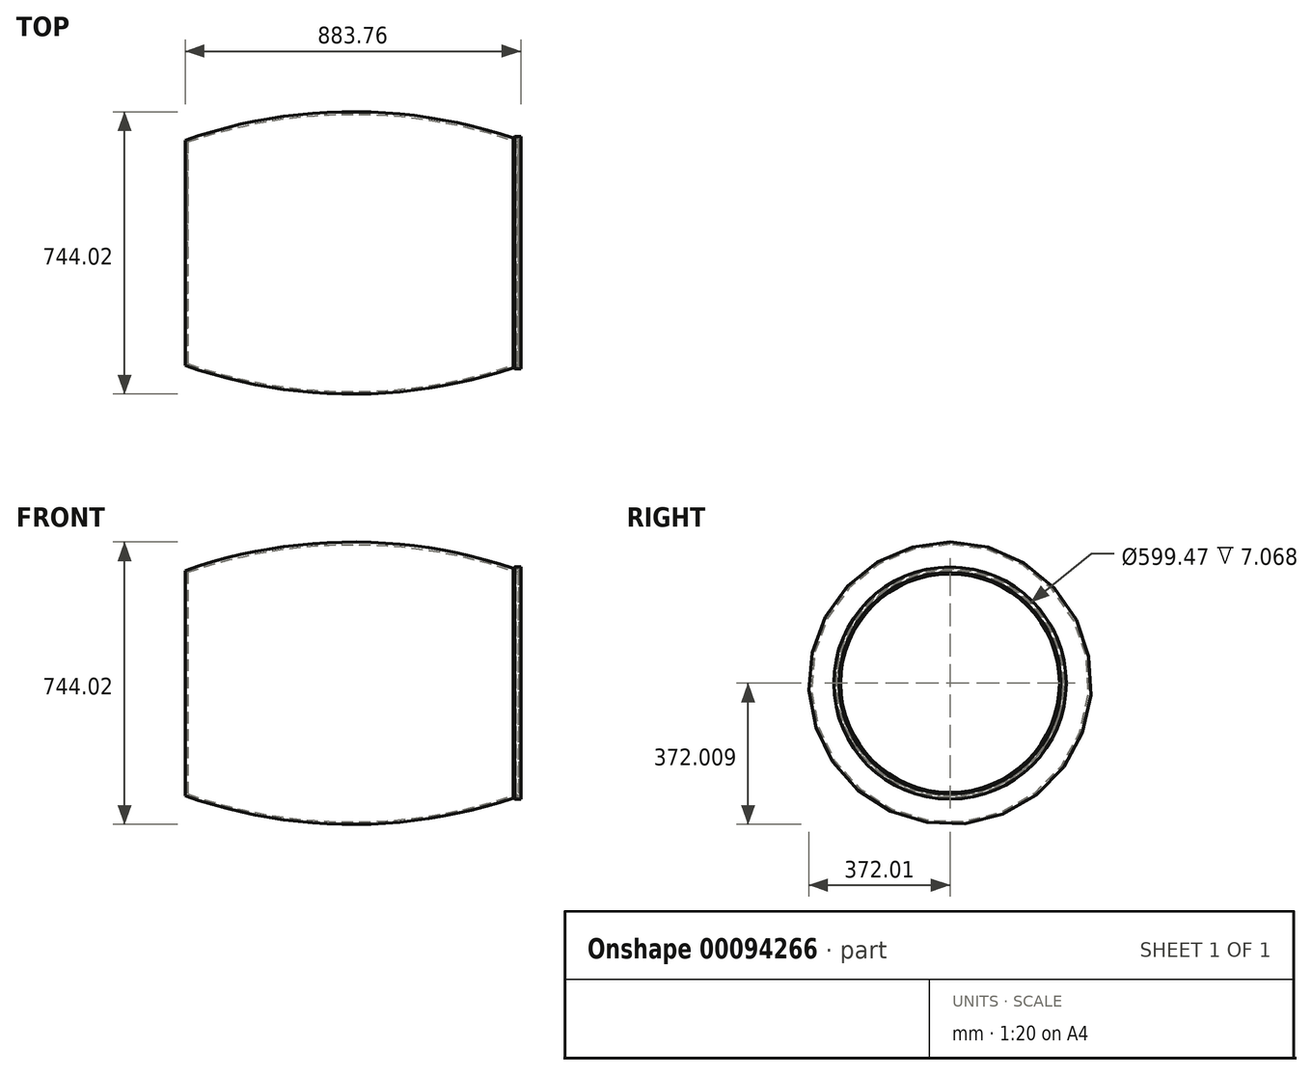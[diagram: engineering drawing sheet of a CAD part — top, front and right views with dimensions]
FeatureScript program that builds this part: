
annotation { "Feature Type Name" : "Feature", "Feature Type Description" : "" }
export const myFeature = defineFeature(function(context is Context, id is Id, definition is map)
    precondition{}
    {
        {
            var Q0;
            Q0=qCreatedBy(makeId("Front.planeOp"),FACE);
            var sketch = newSketch(context, id + "F0", { "sketchPlane" : qUnion([Q0])});
            skLineSegment(sketch, "E0", {"start": v(-396.66, -91.94) * mm, "end": v(466.94, -91.94) * mm});
            skLineSegment(sketch, "E1", {"start": v(466.94, -91.94) * mm, "end": v(466.94, 200.16) * mm});
            skLineSegment(sketch, "E2", {"start": v(-396.66, -91.94) * mm, "end": v(-396.66, 200.16) * mm});
            skLineSegment(sketch, "E3", {"start": v(466.94, 200.16) * mm, "end": v(474.4, 203.75) * mm});
            skLineSegment(sketch, "E4", {"start": v(474.4, 203.75) * mm, "end": v(474.4, 207.8) * mm});
            skLineSegment(sketch, "E5", {"start": v(474.4, 207.8) * mm, "end": v(467.33, 207.8) * mm});
            skLineSegment(sketch, "E6", {"start": v(467.33, 207.8) * mm, "end": v(463.3, 203.17) * mm});
            skArc(sketch, "E7", {"start": v(463.3, 203.17) * mm, "mid": v(33.07, 273.7) * mm, "end": v(-396.66, 200.16) * mm});
            skLineSegment(sketch, "E8.0", {"start": v(-403, -91.94) * mm, "end": v(-403, 204.66) * mm});
            skArc(sketch, "E8.1", {"start": v(461.31, 210.55) * mm, "mid": v(28.66, 280.04) * mm, "end": v(-403, 204.66) * mm});
            skLineSegment(sketch, "E8.2", {"start": v(464.44, 214.14) * mm, "end": v(461.31, 210.55) * mm});
            skLineSegment(sketch, "E8.3", {"start": v(473.3, -91.94) * mm, "end": v(473.3, 196.17) * mm});
            skLineSegment(sketch, "E8.4", {"start": v(473.3, 196.17) * mm, "end": v(480.75, 199.76) * mm});
            skLineSegment(sketch, "E8.5", {"start": v(480.75, 199.76) * mm, "end": v(480.75, 214.14) * mm});
            skLineSegment(sketch, "E8.6", {"start": v(480.75, 214.14) * mm, "end": v(464.44, 214.14) * mm});
            skLineSegment(sketch, "E9", {"start": v(466.94, -91.94) * mm, "end": v(473.3, -91.94) * mm});
            skLineSegment(sketch, "E10", {"start": v(-403, -91.94) * mm, "end": v(-396.66, -91.94) * mm});
            skSolve(sketch);
        }
        {
            var Q0;
            Q0=makeQuery(id+"F0.imprint","IMPRINT",FACE,{"disambiguationData":[TD([[makeQuery(id+"F0.imprint","IMPRINT",EDGE,{"derivedFrom":sQuery(id+"F0.wireOp",EDGE,"E1")}),-1.0]])]});
            var Q1;
            Q1=sQuery(id+"F0.wireOp",EDGE,"E0");
            var Q2;
            Q2=sQuery(id+"F0.wireOp",EDGE,"E0");
            revolve(context, id + "F1", {"entities" : qUnion([Q0]), "surfaceEntities" : qUnion([Q1]), "axis" : qUnion([Q2]), "revolveType" : RevolveType.FULL});
        }
    });
